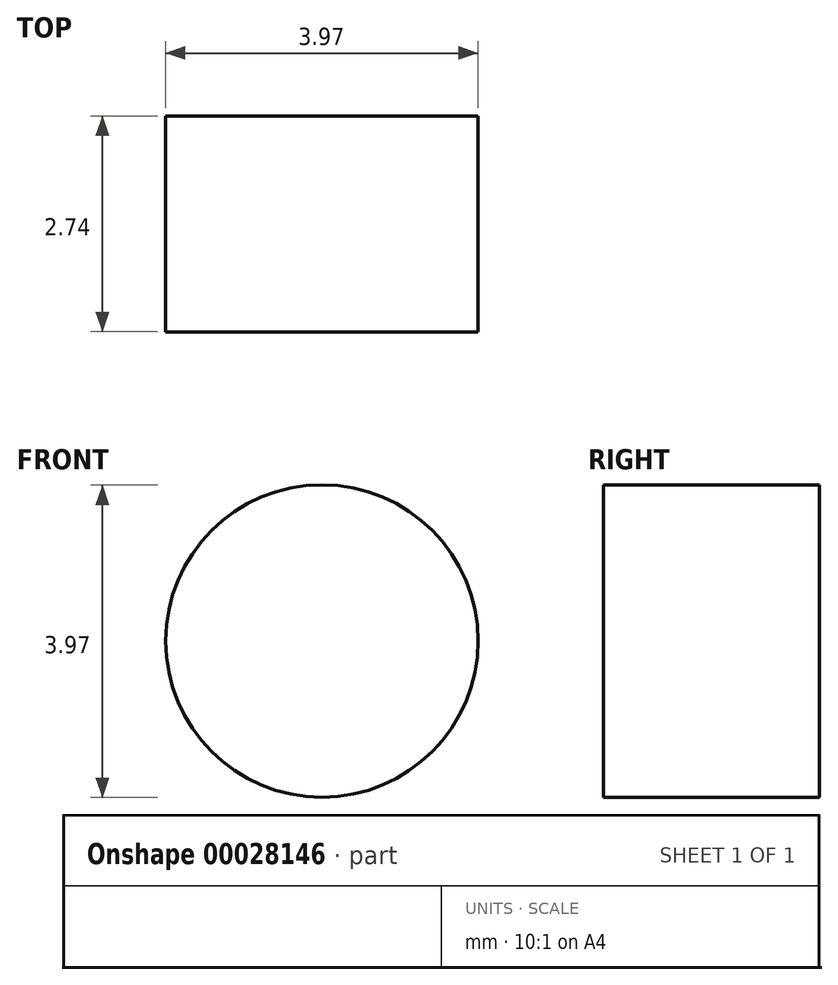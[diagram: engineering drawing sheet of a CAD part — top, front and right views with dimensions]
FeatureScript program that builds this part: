
annotation { "Feature Type Name" : "Feature", "Feature Type Description" : "" }
export const myFeature = defineFeature(function(context is Context, id is Id, definition is map)
    precondition{}
    {
        {
            var Q0;
            Q0=qCreatedBy(makeId("Front.planeOp"),FACE);
            var sketch = newSketch(context, id + "F0", { "sketchPlane" : qUnion([Q0])});
            skCircle(sketch, "E0.MirrorC", {"center": v(-25.94, -9) * mm, "radius": 1.98 * mm});
            skCircle(sketch, "E1.MirrorC", {"center": v(-13.24, -9) * mm, "radius": 1.98 * mm});
            skCircle(sketch, "E2.MirrorC", {"center": v(18.58, -40.77) * mm, "radius": 1.98 * mm});
            skCircle(sketch, "E3.MirrorC", {"center": v(-32.22, -28.05) * mm, "radius": 1.98 * mm});
            skCircle(sketch, "E4.MirrorC", {"center": v(50.33, -34.4) * mm, "radius": 1.98 * mm});
            skCircle(sketch, "E5.MirrorC", {"center": v(69.3, -15.4) * mm, "radius": 1.98 * mm});
            skCircle(sketch, "E6.MirrorC", {"center": v(37.55, -21.73) * mm, "radius": 1.98 * mm});
            skCircle(sketch, "E7.MirrorC", {"center": v(5.88, -28.07) * mm, "radius": 1.98 * mm});
            skCircle(sketch, "E8.MirrorC", {"center": v(-6.82, -28.06) * mm, "radius": 1.98 * mm});
            skCircle(sketch, "E9.MirrorC", {"center": v(-38.57, -34.42) * mm, "radius": 1.98 * mm});
            skCircle(sketch, "E10.MirrorC", {"center": v(43.98, -40.72) * mm, "radius": 1.98 * mm});
            skCircle(sketch, "E11.MirrorC", {"center": v(82, -15.4) * mm, "radius": 1.98 * mm});
            skCircle(sketch, "E12.MirrorC", {"center": v(-64.05, -21.68) * mm, "radius": 1.98 * mm});
            skCircle(sketch, "E13.MirrorC", {"center": v(-76.75, -34.38) * mm, "radius": 1.98 * mm});
            skCircle(sketch, "E14.MirrorC", {"center": v(43.9, -15.38) * mm, "radius": 1.98 * mm});
            skCircle(sketch, "E15.MirrorC", {"center": v(62.95, -21.74) * mm, "radius": 1.98 * mm});
            skCircle(sketch, "E16.MirrorC", {"center": v(-0.47, -34.44) * mm, "radius": 1.98 * mm});
            skCircle(sketch, "E17.MirrorC", {"center": v(-76.74, -8.98) * mm, "radius": 1.98 * mm});
            skCircle(sketch, "E18.MirrorC", {"center": v(75.65, -21.75) * mm, "radius": 1.98 * mm});
            skCircle(sketch, "E19.MirrorC", {"center": v(-64.04, -8.98) * mm, "radius": 1.98 * mm});
            skCircle(sketch, "E20.MirrorC", {"center": v(43.98, -28.08) * mm, "radius": 1.98 * mm});
            skCircle(sketch, "E21.MirrorC", {"center": v(-38.65, -21.7) * mm, "radius": 1.98 * mm});
            skCircle(sketch, "E22.MirrorC", {"center": v(-6.9, -15.36) * mm, "radius": 1.98 * mm});
            skCircle(sketch, "E23.MirrorC", {"center": v(69.38, -40.8) * mm, "radius": 1.98 * mm});
            skCircle(sketch, "E24.MirrorC", {"center": v(-70.32, -28.03) * mm, "radius": 1.98 * mm});
            skCircle(sketch, "E25.MirrorC", {"center": v(12.23, -34.44) * mm, "radius": 1.98 * mm});
            skCircle(sketch, "E26.MirrorC", {"center": v(-19.52, -40.75) * mm, "radius": 1.98 * mm});
            skCircle(sketch, "E27.MirrorC", {"center": v(31.2, -15.35) * mm, "radius": 1.98 * mm});
            skCircle(sketch, "E28.MirrorC", {"center": v(-70.4, -15.33) * mm, "radius": 1.98 * mm});
            skCircle(sketch, "E29.MirrorC", {"center": v(69.38, -28.1) * mm, "radius": 1.98 * mm});
            skCircle(sketch, "E30.MirrorC", {"center": v(-38.64, -9) * mm, "radius": 1.98 * mm});
            skLineSegment(sketch, "E31.MirrorCS", {"start": v(-8.3, -0.5) * mm, "end": v(12.02, -0.56) * mm});
            skCircle(sketch, "E32.MirrorC", {"center": v(5.88, -40.77) * mm, "radius": 1.98 * mm});
            skCircle(sketch, "E33.MirrorC", {"center": v(37.63, -34.45) * mm, "radius": 1.98 * mm});
            skLineSegment(sketch, "E34.MirrorCS", {"start": v(-87.06, -47.07) * mm, "end": v(90.74, -47.15) * mm});
            skCircle(sketch, "E35.MirrorC", {"center": v(50.26, -9.04) * mm, "radius": 1.98 * mm});
            skCircle(sketch, "E36.MirrorC", {"center": v(62.96, -9.04) * mm, "radius": 1.98 * mm});
            skCircle(sketch, "E37.MirrorC", {"center": v(-0.55, -21.71) * mm, "radius": 1.98 * mm});
            skCircle(sketch, "E38.MirrorC", {"center": v(-63.97, -34.4) * mm, "radius": 1.98 * mm});
            skCircle(sketch, "E39.MirrorC", {"center": v(-57.7, -15.34) * mm, "radius": 1.98 * mm});
            skCircle(sketch, "E40.MirrorC", {"center": v(-25.95, -21.7) * mm, "radius": 1.98 * mm});
            skCircle(sketch, "E41.MirrorC", {"center": v(5.8, -15.37) * mm, "radius": 1.98 * mm});
            skCircle(sketch, "E42.MirrorC", {"center": v(82.08, -28.1) * mm, "radius": 1.98 * mm});
            skCircle(sketch, "E43.MirrorC", {"center": v(82.08, -40.8) * mm, "radius": 1.98 * mm});
            skCircle(sketch, "E44.MirrorC", {"center": v(24.93, -34.45) * mm, "radius": 1.98 * mm});
            skCircle(sketch, "E45.MirrorC", {"center": v(12.15, -21.72) * mm, "radius": 1.98 * mm});
            skCircle(sketch, "E46.MirrorC", {"center": v(63.03, -34.4) * mm, "radius": 1.98 * mm});
            skCircle(sketch, "E47.MirrorC", {"center": v(-6.82, -40.76) * mm, "radius": 1.98 * mm});
            skCircle(sketch, "E48.MirrorC", {"center": v(-51.27, -34.41) * mm, "radius": 1.98 * mm});
            skCircle(sketch, "E49.MirrorC", {"center": v(-83.1, -15.33) * mm, "radius": 1.98 * mm});
            skCircle(sketch, "E50.MirrorC", {"center": v(-44.92, -40.74) * mm, "radius": 1.98 * mm});
            skCircle(sketch, "E51.MirrorC", {"center": v(-19.52, -28.05) * mm, "radius": 1.98 * mm});
            skCircle(sketch, "E52.MirrorC", {"center": v(-25.87, -34.43) * mm, "radius": 1.98 * mm});
            skLineSegment(sketch, "E53.MirrorCS", {"start": v(-87.04, -0.65) * mm, "end": v(-76.88, -0.66) * mm});
            skCircle(sketch, "E54.MirrorC", {"center": v(-76.75, -21.68) * mm, "radius": 1.98 * mm});
            skCircle(sketch, "E55.MirrorC", {"center": v(56.6, -15.39) * mm, "radius": 1.98 * mm});
            skLineSegment(sketch, "E56.MirrorCS", {"start": v(80.6, -0.54) * mm, "end": v(90.76, -0.55) * mm});
            skCircle(sketch, "E57.MirrorC", {"center": v(24.85, -21.72) * mm, "radius": 1.98 * mm});
            skCircle(sketch, "E58.MirrorC", {"center": v(12.16, -9.02) * mm, "radius": 1.98 * mm});
            skCircle(sketch, "E59.MirrorC", {"center": v(31.28, -28.08) * mm, "radius": 1.98 * mm});
            skCircle(sketch, "E60.MirrorC", {"center": v(-19.6, -15.35) * mm, "radius": 1.98 * mm});
            skCircle(sketch, "E61.MirrorC", {"center": v(-32.22, -40.75) * mm, "radius": 1.98 * mm});
            skCircle(sketch, "E62.MirrorC", {"center": v(-51.35, -21.7) * mm, "radius": 1.98 * mm});
            skCircle(sketch, "E63.MirrorC", {"center": v(-57.62, -28.04) * mm, "radius": 1.98 * mm});
            skCircle(sketch, "E64.MirrorC", {"center": v(56.68, -40.72) * mm, "radius": 1.98 * mm});
            skCircle(sketch, "E65.MirrorC", {"center": v(24.86, -9.02) * mm, "radius": 1.98 * mm});
            skCircle(sketch, "E66.MirrorC", {"center": v(37.56, -9.03) * mm, "radius": 1.98 * mm});
            skCircle(sketch, "E67.MirrorC", {"center": v(31.28, -40.78) * mm, "radius": 1.98 * mm});
            skCircle(sketch, "E68.MirrorC", {"center": v(-51.34, -9) * mm, "radius": 1.98 * mm});
            skCircle(sketch, "E69.MirrorC", {"center": v(18.58, -28.07) * mm, "radius": 1.98 * mm});
            skCircle(sketch, "E70.MirrorC", {"center": v(-45, -15.34) * mm, "radius": 1.98 * mm});
            skCircle(sketch, "E71.MirrorC", {"center": v(50.25, -21.74) * mm, "radius": 1.98 * mm});
            skCircle(sketch, "E72.MirrorC", {"center": v(-13.17, -34.43) * mm, "radius": 1.98 * mm});
            skCircle(sketch, "E73.MirrorC", {"center": v(-32.3, -15.35) * mm, "radius": 1.98 * mm});
            skCircle(sketch, "E74.MirrorC", {"center": v(75.66, -9.05) * mm, "radius": 1.98 * mm});
            skCircle(sketch, "E75.MirrorC", {"center": v(-0.54, -9.01) * mm, "radius": 1.98 * mm});
            skCircle(sketch, "E76.MirrorC", {"center": v(56.68, -28.09) * mm, "radius": 1.98 * mm});
            skCircle(sketch, "E77.MirrorC", {"center": v(-44.92, -28.04) * mm, "radius": 1.98 * mm});
            skCircle(sketch, "E78.MirrorC", {"center": v(-83.1, -40.73) * mm, "radius": 1.98 * mm});
            skCircle(sketch, "E79.MirrorC", {"center": v(75.73, -34.47) * mm, "radius": 1.98 * mm});
            skCircle(sketch, "E80.MirrorC", {"center": v(-57.62, -40.74) * mm, "radius": 1.98 * mm});
            skCircle(sketch, "E81.MirrorC", {"center": v(-13.25, -21.7) * mm, "radius": 1.98 * mm});
            skCircle(sketch, "E82.MirrorC", {"center": v(-70.4, -40.73) * mm, "radius": 1.98 * mm});
            skCircle(sketch, "E83.MirrorC", {"center": v(-83.1, -28.03) * mm, "radius": 1.98 * mm});
            skCircle(sketch, "E84.MirrorC", {"center": v(18.5, -15.37) * mm, "radius": 1.98 * mm});
            skLineSegment(sketch, "E85.MirrorCS", {"start": v(90.74, -47.15) * mm, "end": v(90.76, -0.55) * mm});
            skLineSegment(sketch, "E86", {"start": v(12.02, -0.56) * mm, "end": v(12.02, 0.81) * mm});
            skLineSegment(sketch, "E87", {"start": v(-8.3, -0.56) * mm, "end": v(-8.3, 0.81) * mm});
            skLineSegment(sketch, "E88.MirrorCS", {"start": v(-8.3, 2.19) * mm, "end": v(-8.3, 0.81) * mm});
            skLineSegment(sketch, "E89.MirrorCS", {"start": v(12.02, 2.19) * mm, "end": v(12.02, 0.81) * mm});
            skCircle(sketch, "E90.MirrorC", {"center": v(-76.75, 23.3) * mm, "radius": 1.98 * mm});
            skCircle(sketch, "E91.MirrorC", {"center": v(56.68, 42.35) * mm, "radius": 1.98 * mm});
            skCircle(sketch, "E92.MirrorC", {"center": v(75.66, 10.68) * mm, "radius": 1.98 * mm});
            skCircle(sketch, "E93.MirrorC", {"center": v(12.16, 10.65) * mm, "radius": 1.98 * mm});
            skCircle(sketch, "E94.MirrorC", {"center": v(-44.92, 42.37) * mm, "radius": 1.98 * mm});
            skCircle(sketch, "E95.MirrorC", {"center": v(-83.1, 16.95) * mm, "radius": 1.98 * mm});
            skCircle(sketch, "E96.MirrorC", {"center": v(24.93, 36.08) * mm, "radius": 1.98 * mm});
            skCircle(sketch, "E97.MirrorC", {"center": v(-51.35, 23.32) * mm, "radius": 1.98 * mm});
            skCircle(sketch, "E98.MirrorC", {"center": v(69.38, 42.42) * mm, "radius": 1.98 * mm});
            skCircle(sketch, "E99.MirrorC", {"center": v(75.73, 36.1) * mm, "radius": 1.98 * mm});
            skCircle(sketch, "E100.MirrorC", {"center": v(-44.92, 29.67) * mm, "radius": 1.98 * mm});
            skCircle(sketch, "E101.MirrorC", {"center": v(82.08, 29.73) * mm, "radius": 1.98 * mm});
            skCircle(sketch, "E102.MirrorC", {"center": v(63.03, 36.03) * mm, "radius": 1.98 * mm});
            skCircle(sketch, "E103.MirrorC", {"center": v(-57.7, 16.97) * mm, "radius": 1.98 * mm});
            skCircle(sketch, "E104.MirrorC", {"center": v(-51.34, 10.62) * mm, "radius": 1.98 * mm});
            skCircle(sketch, "E105.MirrorC", {"center": v(-32.22, 42.38) * mm, "radius": 1.98 * mm});
            skCircle(sketch, "E106.MirrorC", {"center": v(-64.05, 23.31) * mm, "radius": 1.98 * mm});
            skCircle(sketch, "E107.MirrorC", {"center": v(37.55, 23.36) * mm, "radius": 1.98 * mm});
            skCircle(sketch, "E108.MirrorC", {"center": v(-76.74, 10.6) * mm, "radius": 1.98 * mm});
            skCircle(sketch, "E109.MirrorC", {"center": v(-70.32, 29.66) * mm, "radius": 1.98 * mm});
            skCircle(sketch, "E110.MirrorC", {"center": v(-76.75, 36) * mm, "radius": 1.98 * mm});
            skCircle(sketch, "E111.MirrorC", {"center": v(-6.82, 29.69) * mm, "radius": 1.98 * mm});
            skCircle(sketch, "E112.MirrorC", {"center": v(82, 17.03) * mm, "radius": 1.98 * mm});
            skCircle(sketch, "E113.MirrorC", {"center": v(-13.25, 23.34) * mm, "radius": 1.98 * mm});
            skCircle(sketch, "E114.MirrorC", {"center": v(24.86, 10.65) * mm, "radius": 1.98 * mm});
            skCircle(sketch, "E115.MirrorC", {"center": v(37.56, 10.66) * mm, "radius": 1.98 * mm});
            skCircle(sketch, "E116.MirrorC", {"center": v(-19.6, 16.98) * mm, "radius": 1.98 * mm});
            skCircle(sketch, "E117.MirrorC", {"center": v(-70.4, 42.36) * mm, "radius": 1.98 * mm});
            skCircle(sketch, "E118.MirrorC", {"center": v(18.5, 17) * mm, "radius": 1.98 * mm});
            skLineSegment(sketch, "E119.MirrorCS", {"start": v(-87.06, 48.7) * mm, "end": v(-87.04, 2.1) * mm});
            skCircle(sketch, "E120.MirrorC", {"center": v(-57.62, 29.67) * mm, "radius": 1.98 * mm});
            skCircle(sketch, "E121.MirrorC", {"center": v(-57.62, 42.37) * mm, "radius": 1.98 * mm});
            skCircle(sketch, "E122.MirrorC", {"center": v(75.65, 23.38) * mm, "radius": 1.98 * mm});
            skCircle(sketch, "E123.MirrorC", {"center": v(-19.52, 42.38) * mm, "radius": 1.98 * mm});
            skCircle(sketch, "E124.MirrorC", {"center": v(50.25, 23.36) * mm, "radius": 1.98 * mm});
            skCircle(sketch, "E125.MirrorC", {"center": v(12.23, 36.07) * mm, "radius": 1.98 * mm});
            skCircle(sketch, "E126.MirrorC", {"center": v(-0.47, 36.06) * mm, "radius": 1.98 * mm});
            skCircle(sketch, "E127.MirrorC", {"center": v(-38.64, 10.62) * mm, "radius": 1.98 * mm});
            skCircle(sketch, "E128.MirrorC", {"center": v(31.2, 16.98) * mm, "radius": 1.98 * mm});
            skCircle(sketch, "E129.MirrorC", {"center": v(-32.3, 16.98) * mm, "radius": 1.98 * mm});
            skCircle(sketch, "E130.MirrorC", {"center": v(56.6, 17.02) * mm, "radius": 1.98 * mm});
            skCircle(sketch, "E131.MirrorC", {"center": v(-32.22, 29.68) * mm, "radius": 1.98 * mm});
            skCircle(sketch, "E132.MirrorC", {"center": v(-13.24, 10.64) * mm, "radius": 1.98 * mm});
            skCircle(sketch, "E133.MirrorC", {"center": v(-25.94, 10.63) * mm, "radius": 1.98 * mm});
            skCircle(sketch, "E134.MirrorC", {"center": v(31.28, 29.7) * mm, "radius": 1.98 * mm});
            skCircle(sketch, "E135.MirrorC", {"center": v(43.98, 42.34) * mm, "radius": 1.98 * mm});
            skCircle(sketch, "E136.MirrorC", {"center": v(-38.57, 36.05) * mm, "radius": 1.98 * mm});
            skCircle(sketch, "E137.MirrorC", {"center": v(-13.17, 36.06) * mm, "radius": 1.98 * mm});
            skCircle(sketch, "E138.MirrorC", {"center": v(-25.87, 36.05) * mm, "radius": 1.98 * mm});
            skCircle(sketch, "E139.MirrorC", {"center": v(-83.1, 29.65) * mm, "radius": 1.98 * mm});
            skCircle(sketch, "E140.MirrorC", {"center": v(-51.27, 36.04) * mm, "radius": 1.98 * mm});
            skCircle(sketch, "E141.MirrorC", {"center": v(-63.97, 36.04) * mm, "radius": 1.98 * mm});
            skLineSegment(sketch, "E142.MirrorCS", {"start": v(-8.3, 2.14) * mm, "end": v(12.02, 2.19) * mm});
            skCircle(sketch, "E143.MirrorC", {"center": v(-19.52, 29.68) * mm, "radius": 1.98 * mm});
            skCircle(sketch, "E144.MirrorC", {"center": v(62.96, 10.67) * mm, "radius": 1.98 * mm});
            skLineSegment(sketch, "E145.MirrorCS", {"start": v(80.6, 2.2) * mm, "end": v(90.76, 2.2) * mm});
            skCircle(sketch, "E146.MirrorC", {"center": v(69.38, 29.72) * mm, "radius": 1.98 * mm});
            skCircle(sketch, "E147.MirrorC", {"center": v(18.58, 29.7) * mm, "radius": 1.98 * mm});
            skLineSegment(sketch, "E148.MirrorCS", {"start": v(90.74, 48.78) * mm, "end": v(90.76, 2.2) * mm});
            skCircle(sketch, "E149.MirrorC", {"center": v(5.88, 42.4) * mm, "radius": 1.98 * mm});
            skCircle(sketch, "E150.MirrorC", {"center": v(31.28, 42.4) * mm, "radius": 1.98 * mm});
            skCircle(sketch, "E151.MirrorC", {"center": v(56.68, 29.72) * mm, "radius": 1.98 * mm});
            skCircle(sketch, "E152.MirrorC", {"center": v(-6.9, 16.99) * mm, "radius": 1.98 * mm});
            skCircle(sketch, "E153.MirrorC", {"center": v(5.8, 17) * mm, "radius": 1.98 * mm});
            skCircle(sketch, "E154.MirrorC", {"center": v(-45, 16.97) * mm, "radius": 1.98 * mm});
            skCircle(sketch, "E155.MirrorC", {"center": v(50.33, 36.02) * mm, "radius": 1.98 * mm});
            skCircle(sketch, "E156.MirrorC", {"center": v(18.58, 42.4) * mm, "radius": 1.98 * mm});
            skCircle(sketch, "E157.MirrorC", {"center": v(-0.55, 23.34) * mm, "radius": 1.98 * mm});
            skLineSegment(sketch, "E158.MirrorCS", {"start": v(-87.06, 48.7) * mm, "end": v(90.74, 48.78) * mm});
            skCircle(sketch, "E159.MirrorC", {"center": v(82.08, 42.43) * mm, "radius": 1.98 * mm});
            skCircle(sketch, "E160.MirrorC", {"center": v(12.15, 23.35) * mm, "radius": 1.98 * mm});
            skCircle(sketch, "E161.MirrorC", {"center": v(5.88, 29.7) * mm, "radius": 1.98 * mm});
            skCircle(sketch, "E162.MirrorC", {"center": v(-64.04, 10.61) * mm, "radius": 1.98 * mm});
            skCircle(sketch, "E163.MirrorC", {"center": v(-38.65, 23.32) * mm, "radius": 1.98 * mm});
            skLineSegment(sketch, "E164.MirrorCS", {"start": v(-87.04, 2.1) * mm, "end": v(-76.88, 2.1) * mm});
            skCircle(sketch, "E165.MirrorC", {"center": v(37.63, 36.08) * mm, "radius": 1.98 * mm});
            skCircle(sketch, "E166.MirrorC", {"center": v(43.98, 29.71) * mm, "radius": 1.98 * mm});
            skCircle(sketch, "E167.MirrorC", {"center": v(-0.54, 10.64) * mm, "radius": 1.98 * mm});
            skCircle(sketch, "E168.MirrorC", {"center": v(-83.1, 42.35) * mm, "radius": 1.98 * mm});
            skCircle(sketch, "E169.MirrorC", {"center": v(-25.95, 23.33) * mm, "radius": 1.98 * mm});
            skCircle(sketch, "E170.MirrorC", {"center": v(24.85, 23.35) * mm, "radius": 1.98 * mm});
            skCircle(sketch, "E171.MirrorC", {"center": v(62.95, 23.37) * mm, "radius": 1.98 * mm});
            skCircle(sketch, "E172.MirrorC", {"center": v(50.26, 10.66) * mm, "radius": 1.98 * mm});
            skCircle(sketch, "E173.MirrorC", {"center": v(-6.82, 42.39) * mm, "radius": 1.98 * mm});
            skCircle(sketch, "E174.MirrorC", {"center": v(-70.4, 16.96) * mm, "radius": 1.98 * mm});
            skCircle(sketch, "E175.MirrorC", {"center": v(43.9, 17.01) * mm, "radius": 1.98 * mm});
            skCircle(sketch, "E176.MirrorC", {"center": v(69.3, 17.02) * mm, "radius": 1.98 * mm});
            skLineSegment(sketch, "E177", {"start": v(-76.88, -0.66) * mm, "end": v(-76.88, 2.1) * mm});
            skLineSegment(sketch, "E178", {"start": v(-87.04, -0.65) * mm, "end": v(-87.06, -47.07) * mm});
            skLineSegment(sketch, "E179", {"start": v(80.6, -0.54) * mm, "end": v(80.6, 2.2) * mm});
            skSolve(sketch);
        }
        {
            var Q0;
            Q0=makeQuery(id+"F0.imprint","IMPRINT",FACE,{"disambiguationData":[TD([[makeQuery(id+"F0.imprint","IMPRINT",EDGE,{"derivedFrom":sQuery(id+"F0.wireOp",EDGE,"E0.MirrorC")}),1.0]])]});
            extrude(context, id + "F1", {"entities" : qUnion([Q0]), "depth" : 2.74 * mm});
        }
    });
